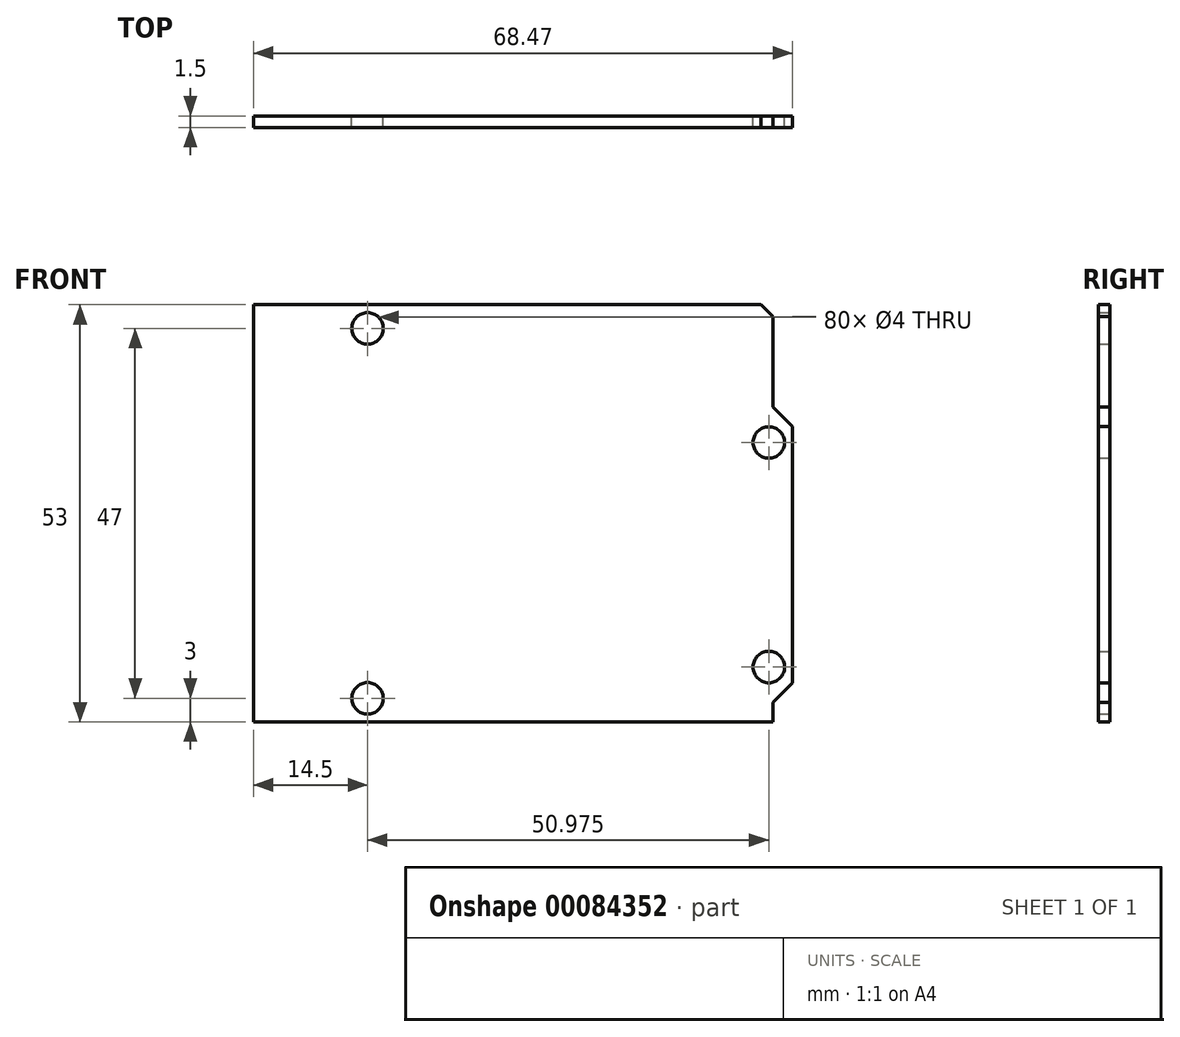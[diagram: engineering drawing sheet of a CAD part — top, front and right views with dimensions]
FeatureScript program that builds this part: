
annotation { "Feature Type Name" : "Feature", "Feature Type Description" : "" }
export const myFeature = defineFeature(function(context is Context, id is Id, definition is map)
    precondition{}
    {
        {
            var Q0;
            Q0=qCreatedBy(makeId("Front.planeOp"),FACE);
            var sketch = newSketch(context, id + "F0", { "sketchPlane" : qUnion([Q0])});
            skLineSegment(sketch, "E0.bottom", {"start": v(0, 0) * mm, "end": v(66, 0) * mm});
            skLineSegment(sketch, "E0.top", {"start": v(0, 53) * mm, "end": v(64.5, 53) * mm});
            skLineSegment(sketch, "E0.left", {"start": v(0, 0) * mm, "end": v(0, 53) * mm});
            skPoint(sketch, "E1", {"position": v(66, 2.5) * mm});
            skPoint(sketch, "E2", {"position": v(66, 40) * mm});
            skLineSegment(sketch, "E3", {"start": v(66, 40) * mm, "end": v(68.47, 37.53) * mm});
            skLineSegment(sketch, "E4", {"start": v(66, 2.5) * mm, "end": v(68.47, 4.97) * mm});
            skLineSegment(sketch, "E5", {"start": v(66, 51.5) * mm, "end": v(66, 40) * mm});
            skLineSegment(sketch, "E6", {"start": v(66, 2.5) * mm, "end": v(66, 0) * mm});
            skLineSegment(sketch, "E7", {"start": v(68.47, 37.53) * mm, "end": v(68.47, 4.97) * mm});
            skPoint(sketch, "E8", {"position": v(66, 51.5) * mm});
            skPoint(sketch, "E9", {"position": v(64.5, 53) * mm});
            skLineSegment(sketch, "E10", {"start": v(64.5, 53) * mm, "end": v(66, 51.5) * mm});
            skPoint(sketch, "E11.orphan", {"position": v(66, 53) * mm});
            skCircle(sketch, "E12", {"center": v(65.47, 6.98) * mm, "radius": 2 * mm});
            skCircle(sketch, "E13", {"center": v(65.47, 35.5) * mm, "radius": 2 * mm});
            skCircle(sketch, "E14", {"center": v(14.5, 50) * mm, "radius": 2 * mm});
            skCircle(sketch, "E15", {"center": v(14.5, 3) * mm, "radius": 2 * mm});
            skLineSegment(sketch, "E16", {"start": v(66, 51.5) * mm, "end": v(66, 49.5) * mm});
            skLineSegment(sketch, "E17", {"start": v(66, 49.5) * mm, "end": v(65, 49.5) * mm});
            skSolve(sketch);
        }
        {
            var Q0;
            Q0=makeQuery(id+"F0.imprint","IMPRINT",FACE,{"disambiguationData":[TD([[makeQuery(id+"F0.imprint","IMPRINT",EDGE,{"derivedFrom":sQuery(id+"F0.wireOp",EDGE,"E0.bottom")}),1.0]])]});
            extrude(context, id + "F1", {"entities" : qUnion([Q0]), "depth" : 1.5 * mm});
        }
    });
